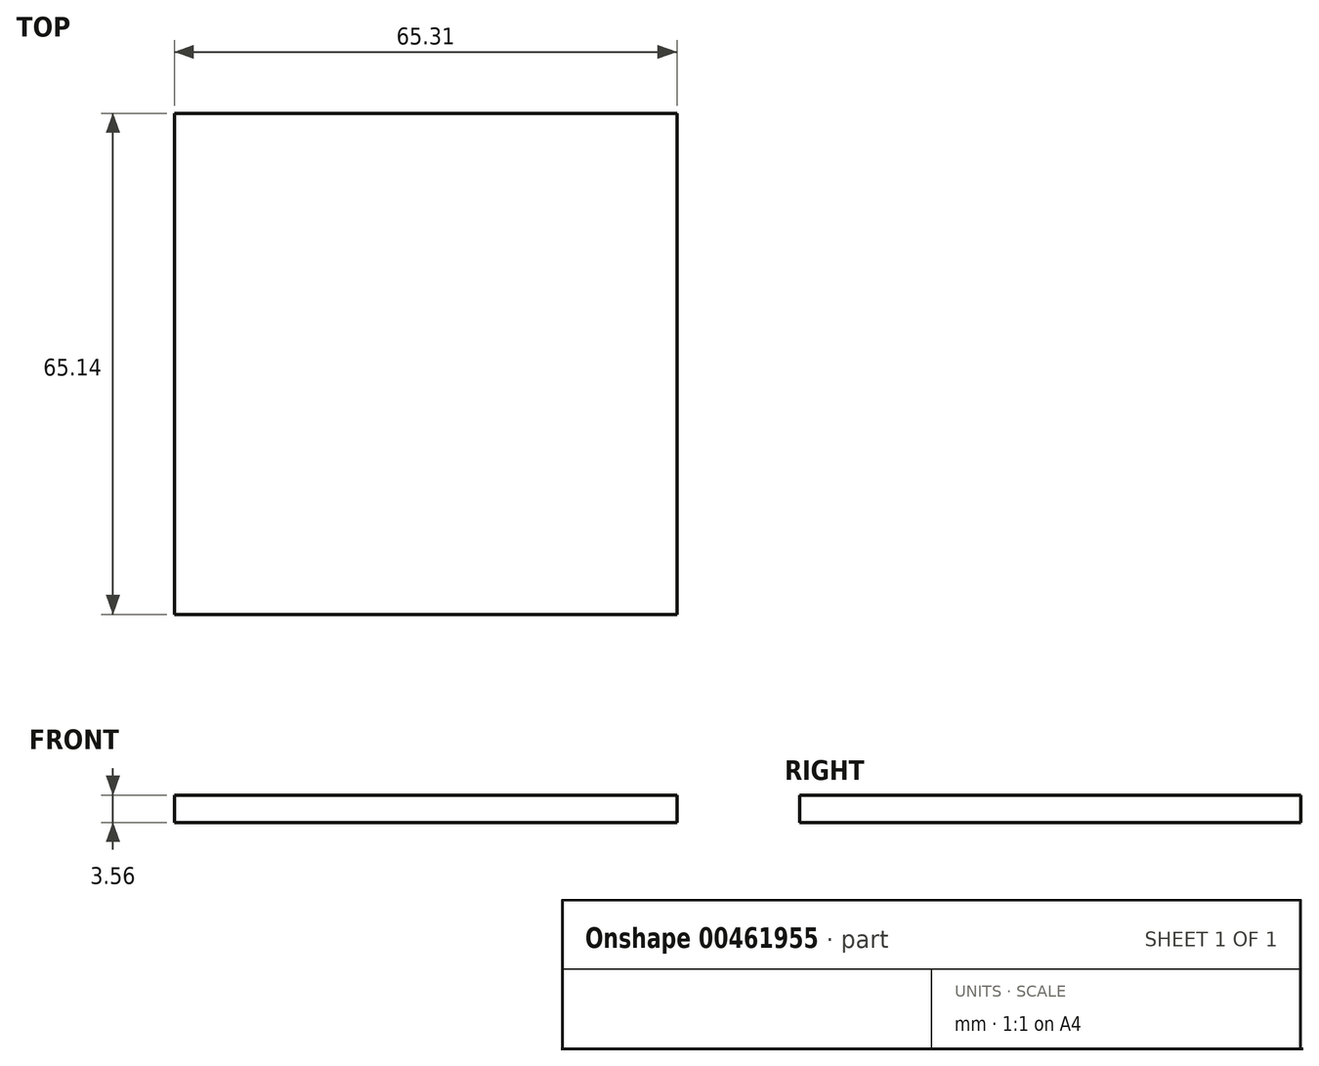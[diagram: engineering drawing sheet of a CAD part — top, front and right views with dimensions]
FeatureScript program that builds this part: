
annotation { "Feature Type Name" : "Feature", "Feature Type Description" : "" }
export const myFeature = defineFeature(function(context is Context, id is Id, definition is map)
    precondition{}
    {
        {
            var Q0;
            Q0=qCreatedBy(makeId("Top.planeOp"),FACE);
            var sketch = newSketch(context, id + "F0", { "sketchPlane" : qUnion([Q0])});
            skSolve(sketch);
        }
        {
            var Q0;
            Q0=qCreatedBy(makeId("Top.planeOp"),FACE);
            var sketch = newSketch(context, id + "F1", { "sketchPlane" : qUnion([Q0])});
            skLineSegment(sketch, "E0.bottom", {"start": v(-132.57, -114.91) * mm, "end": v(-197.88, -114.91) * mm});
            skLineSegment(sketch, "E0.top", {"start": v(-132.57, -49.77) * mm, "end": v(-197.88, -49.77) * mm});
            skLineSegment(sketch, "E0.left", {"start": v(-132.57, -114.91) * mm, "end": v(-132.57, -49.77) * mm});
            skLineSegment(sketch, "E0.right", {"start": v(-197.88, -114.91) * mm, "end": v(-197.88, -49.77) * mm});
            skPoint(sketch, "E0.middle", {"position": v(-165.23, -82.34) * mm});
            skSolve(sketch);
        }
        {
            var Q0;
            Q0 = qSketchRegion(id + "F0", true);
            var Q1;
            Q1=makeQuery(id+"F1.imprint","IMPRINT",FACE,{"disambiguationData":[TD([[makeQuery(id+"F1.imprint","IMPRINT",EDGE,{"derivedFrom":sQuery(id+"F1.wireOp",EDGE,"E0.bottom")}),-1.0]])]});
            extrude(context, id + "F2", {"entities" : qUnion([Q0, Q1]), "depth" : 3.56 * mm});
        }
    });
